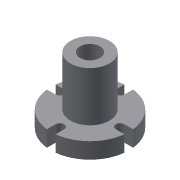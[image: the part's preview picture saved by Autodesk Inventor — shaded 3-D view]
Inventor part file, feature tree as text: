
AUTODESK INVENTOR PART (.ipt)
format: ipt  version: 2014 (Build 180170000, 170)  size: 111,616 bytes
history: native  units: mm
features: extrude x3, sketch x3, pattern_circular x1
ambient origin geometry x8: Origin, YZ Plane, XZ Plane, XY Plane, X Axis, Y Axis, Z Axis, Center Point
bodies: Solid1 (feature_tree)
feature tree (7):
  extrude  "Extrusion1"  Depth=8.1mm
  extrude  "Extrusion2"  Depth=6.46mm
  extrude  "Extrusion3"  Depth=3.5mm
  pattern_circular  "Circular Pattern1"  [2 undecoded]
  sketch  "Sketch1"  dims[d0=31.5mm d1=8.1mm]
  sketch  "Sketch2"  dims[d2=6.46mm d3=0.0mm d4=15.8mm]
  sketch  "Sketch3"  dims[d5=20.0mm d6=0.0mm d7=3.5mm d8=3.5mm d9=20.0mm d10=0.0mm d11=40.0mm d12=360.0deg]
note: 2 required parameter values undecoded (feature->parameter linkage not recoverable at this tier; creation-order binding heuristic only, values carry confidence <= 0.55)
